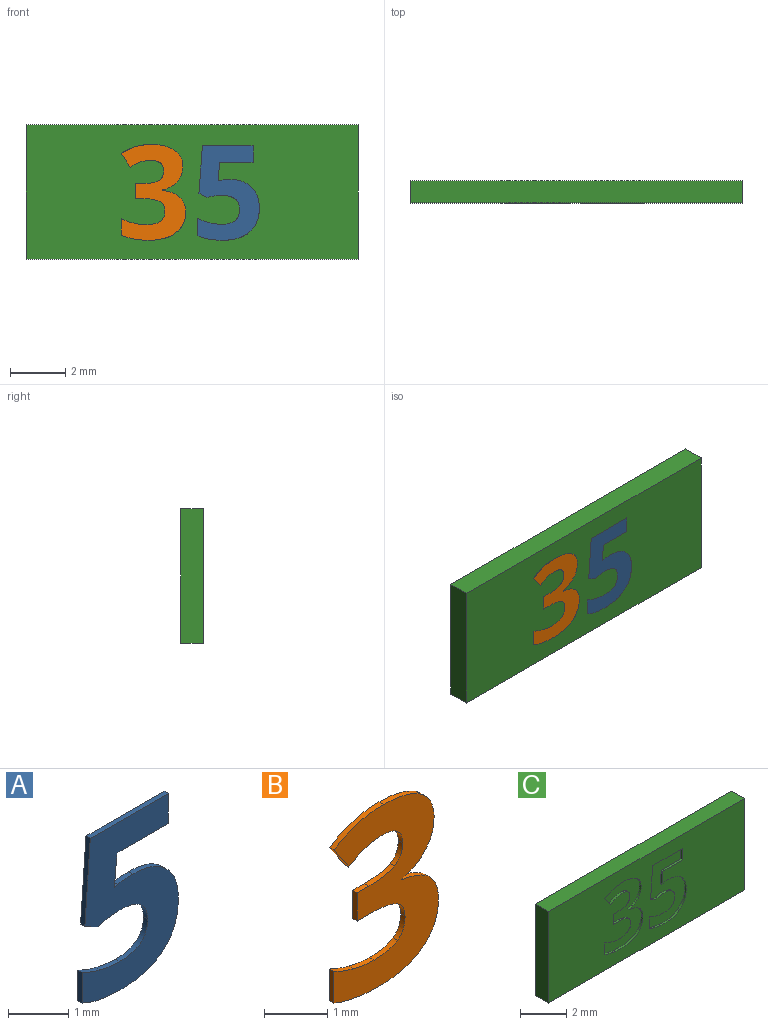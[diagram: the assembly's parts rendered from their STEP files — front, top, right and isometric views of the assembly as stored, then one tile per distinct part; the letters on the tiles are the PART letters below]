
ASSEMBLY  parts=3 mates=2
PART A: 22 faces, bbox 2.3x0.1x3.4 mm
  f0: plane 3.42x2.25mm, normal (0,-1,0), area 4.5mm2, adj f1,f2,f3,f4,f5,f6,f7,f8
  f1: plane 0.1x0.08mm, normal (-0.2,0,0.98), area 0mm2, adj f0,f2,f18,f20
  f2: plane 0.66x0.1mm, normal (1,0,-0.09), area 0.1mm2, adj f0,f1,f3,f18
  f3: plane 1.2x0.1mm, normal (0,0,-1), area 0.1mm2, adj f0,f2,f4,f18
  f4: plane 0.6x0.1mm, normal (1,0,0), area 0.1mm2, adj f0,f3,f5,f18
  f5: plane 1.83x0.1mm, normal (0,0,1), area 0.2mm2, adj f0,f4,f6,f18
  f6: plane 1.72x0.13mm, normal (-1,0,0.07), area 0.2mm2, adj f0,f5,f7,f18
  f7: plane 0.28x0.15mm, normal (-0.47,0,-0.88), area 0mm2, adj f0,f6,f8,f18
  f8: extruded ~0.24x0.1mm, area 0mm2, adj f0,f7,f9,f18
  f9: extruded ~0.27x0.1mm, area 0mm2, adj f0,f8,f10,f18
  f10: extruded ~0.68x0.51mm, area 0.1mm2, adj f0,f9,f11,f18
  f11: extruded ~0.65x0.54mm, area 0.1mm2, adj f0,f10,f12,f18
  f12: extruded ~0.46x0.1mm, area 0mm2, adj f0,f11,f13,f18
  f13: extruded ~0.42x0.16mm, area 0mm2, adj f0,f12,f14,f18
  f14: plane 0.62x0.1mm, normal (-1,0,0), area 0.1mm2, adj f0,f13,f15,f18
  f15: extruded ~0.91x0.18mm, area 0.1mm2, adj f0,f14,f16,f18
  f16: extruded ~1x0.3mm, area 0.1mm2, adj f0,f15,f17,f18
  f17: extruded ~0.87x0.35mm, area 0.1mm2, adj f0,f16,f18,f19
  f18: plane 3.42x2.25mm, normal (0,1,0), area 4.5mm2, adj f1,f2,f3,f4,f5,f6,f7,f8
  f19: extruded ~0.75x0.29mm, area 0.1mm2, adj f0,f17,f18,f21
  f20: extruded ~0.35x0.1mm, area 0mm2, adj f0,f1,f18,f21
  f21: extruded ~0.78x0.27mm, area 0.1mm2, adj f0,f18,f19,f20
PART B: 29 faces, bbox 2.3x0.1x3.5 mm
  f0: plane 3.47x2.33mm, normal (0,-1,0), area 4.3mm2, adj f1,f2,f3,f4,f5,f6,f7,f8
  f1: extruded ~0.83x0.21mm, area 0.1mm2, adj f0,f2,f25,f27
  f2: extruded ~1.1x0.33mm, area 0.1mm2, adj f0,f1,f3,f25
  f3: plane 0.49x0.33mm, normal (-0.83,0,-0.56), area 0.1mm2, adj f0,f2,f4,f25
  f4: extruded ~0.38x0.19mm, area 0mm2, adj f0,f3,f5,f25
  f5: extruded ~0.34x0.1mm, area 0mm2, adj f0,f4,f6,f25
  f6: extruded ~0.48x0.38mm, area 0.1mm2, adj f0,f5,f7,f25
  f7: extruded ~0.35x0.18mm, area 0mm2, adj f0,f6,f8,f25
  f8: extruded ~0.57x0.1mm, area 0.1mm2, adj f0,f7,f9,f25
  f9: plane 0.26x0.1mm, normal (0,0,1), area 0mm2, adj f0,f8,f10,f25
  f10: plane 0.55x0.1mm, normal (-1,0,0), area 0.1mm2, adj f0,f9,f11,f25
  f11: plane 0.26x0.1mm, normal (0,0,-1), area 0mm2, adj f0,f10,f12,f25
  f12: extruded ~0.62x0.1mm, area 0.1mm2, adj f0,f11,f13,f25
  f13: extruded ~0.34x0.19mm, area 0mm2, adj f0,f12,f14,f25
  f14: extruded ~0.39x0.17mm, area 0mm2, adj f0,f13,f15,f25
  f15: extruded ~0.52x0.12mm, area 0.1mm2, adj f0,f14,f16,f25
  f16: extruded ~0.47x0.1mm, area 0mm2, adj f0,f15,f17,f25
  f17: extruded ~0.43x0.16mm, area 0mm2, adj f0,f16,f18,f25
  f18: plane 0.61x0.1mm, normal (-1,0,0), area 0.1mm2, adj f0,f17,f19,f25
  f19: extruded ~0.97x0.18mm, area 0.1mm2, adj f0,f18,f20,f25
  f20: extruded ~1.01x0.27mm, area 0.1mm2, adj f0,f19,f21,f25
  f21: extruded ~0.76x0.35mm, area 0.1mm2, adj f0,f20,f22,f25
  f22: extruded ~0.53x0.21mm, area 0.1mm2, adj f0,f21,f23,f25
  f23: extruded ~0.62x0.25mm, area 0.1mm2, adj f0,f22,f24,f25
  f24: plane 0.1x0.01mm, normal (1,0,0), area 0mm2, adj f0,f23,f25,f26
  f25: plane 3.47x2.33mm, normal (0,1,0), area 4.3mm2, adj f1,f2,f3,f4,f5,f6,f7,f8
  f26: extruded ~0.54x0.3mm, area 0.1mm2, adj f0,f24,f25,f28
  f27: extruded ~0.59x0.3mm, area 0.1mm2, adj f0,f1,f25,f28
  f28: extruded ~0.54x0.19mm, area 0.1mm2, adj f0,f25,f26,f27
PART C: 55 faces, bbox 12x0.8x4.9 mm
  f0: plane 12x4.85mm, normal (0,-1,0), area 49.4mm2, adj f1,f2,f3,f4,f6,f7,f8,f9
  f1: plane 12x0.8mm, normal (0,0,-1), area 9.6mm2, adj f0,f2,f4,f5
  f2: plane 4.85x0.8mm, normal (1,0,0), area 3.9mm2, adj f0,f1,f3,f5
  f3: plane 12x0.8mm, normal (0,0,1), area 9.6mm2, adj f0,f2,f4,f5
  f4: plane 4.85x0.8mm, normal (-1,0,0), area 3.9mm2, adj f0,f1,f3,f5
  f5: plane 12x4.85mm, normal (0,1,0), area 58.2mm2, adj f1,f2,f3,f4
  f6: extruded ~0.35x0.1mm, area 0mm2, adj f0,f7,f25,f26
  f7: plane 0.1x0.08mm, normal (0.2,0,-0.98), area 0mm2, adj f0,f6,f8,f26
  f8: plane 0.66x0.1mm, normal (-1,0,0.09), area 0.1mm2, adj f0,f7,f9,f26
  f9: plane 1.2x0.1mm, normal (0,0,1), area 0.1mm2, adj f0,f8,f10,f26
  f10: plane 0.6x0.1mm, normal (-1,0,0), area 0.1mm2, adj f0,f9,f11,f26
  f11: plane 1.83x0.1mm, normal (0,0,-1), area 0.2mm2, adj f0,f10,f12,f26
  f12: plane 1.72x0.13mm, normal (1,0,-0.07), area 0.2mm2, adj f0,f11,f13,f26
  f13: plane 0.28x0.15mm, normal (0.47,0,0.88), area 0mm2, adj f0,f12,f14,f26
  f14: extruded ~0.24x0.1mm, area 0mm2, adj f0,f13,f15,f26
  f15: extruded ~0.27x0.1mm, area 0mm2, adj f0,f14,f16,f26
  f16: extruded ~0.68x0.51mm, area 0.1mm2, adj f0,f15,f17,f26
  f17: extruded ~0.65x0.54mm, area 0.1mm2, adj f0,f16,f18,f26
  f18: extruded ~0.46x0.1mm, area 0mm2, adj f0,f17,f19,f26
  f19: extruded ~0.42x0.16mm, area 0mm2, adj f0,f18,f20,f26
  f20: plane 0.62x0.1mm, normal (1,0,0), area 0.1mm2, adj f0,f19,f21,f26
  f21: extruded ~0.91x0.18mm, area 0.1mm2, adj f0,f20,f22,f26
  f22: extruded ~1x0.3mm, area 0.1mm2, adj f0,f21,f23,f26
  f23: extruded ~0.87x0.35mm, area 0.1mm2, adj f0,f22,f24,f26
  f24: extruded ~0.75x0.29mm, area 0.1mm2, adj f0,f23,f25,f26
  f25: extruded ~0.78x0.27mm, area 0.1mm2, adj f0,f6,f24,f26
  f26: plane 3.42x2.25mm, normal (0,-1,0), area 4.5mm2, adj f6,f7,f8,f9,f10,f11,f12,f13
  f27: extruded ~0.59x0.3mm, area 0.1mm2, adj f0,f28,f53,f54
  f28: extruded ~0.83x0.21mm, area 0.1mm2, adj f0,f27,f29,f54
  f29: extruded ~1.1x0.33mm, area 0.1mm2, adj f0,f28,f30,f54
  f30: plane 0.49x0.33mm, normal (0.83,0,0.56), area 0.1mm2, adj f0,f29,f31,f54
  f31: extruded ~0.38x0.19mm, area 0mm2, adj f0,f30,f32,f54
  f32: extruded ~0.34x0.1mm, area 0mm2, adj f0,f31,f33,f54
  f33: extruded ~0.48x0.38mm, area 0.1mm2, adj f0,f32,f34,f54
  f34: extruded ~0.35x0.18mm, area 0mm2, adj f0,f33,f35,f54
  f35: extruded ~0.57x0.1mm, area 0.1mm2, adj f0,f34,f36,f54
  f36: plane 0.26x0.1mm, normal (0,0,-1), area 0mm2, adj f0,f35,f37,f54
  f37: plane 0.55x0.1mm, normal (1,0,0), area 0.1mm2, adj f0,f36,f38,f54
  f38: plane 0.26x0.1mm, normal (0,0,1), area 0mm2, adj f0,f37,f39,f54
  f39: extruded ~0.62x0.1mm, area 0.1mm2, adj f0,f38,f40,f54
  f40: extruded ~0.34x0.19mm, area 0mm2, adj f0,f39,f41,f54
  f41: extruded ~0.39x0.17mm, area 0mm2, adj f0,f40,f42,f54
  f42: extruded ~0.52x0.12mm, area 0.1mm2, adj f0,f41,f43,f54
  f43: extruded ~0.47x0.1mm, area 0mm2, adj f0,f42,f44,f54
  f44: extruded ~0.43x0.16mm, area 0mm2, adj f0,f43,f45,f54
  f45: plane 0.61x0.1mm, normal (1,0,0), area 0.1mm2, adj f0,f44,f46,f54
  f46: extruded ~0.97x0.18mm, area 0.1mm2, adj f0,f45,f47,f54
  f47: extruded ~1.01x0.27mm, area 0.1mm2, adj f0,f46,f48,f54
  f48: extruded ~0.76x0.35mm, area 0.1mm2, adj f0,f47,f49,f54
  f49: extruded ~0.53x0.21mm, area 0.1mm2, adj f0,f48,f50,f54
  f50: extruded ~0.62x0.25mm, area 0.1mm2, adj f0,f49,f51,f54
  f51: plane 0.1x0.01mm, normal (-1,0,0), area 0mm2, adj f0,f50,f52,f54
  f52: extruded ~0.54x0.3mm, area 0.1mm2, adj f0,f51,f53,f54
  f53: extruded ~0.54x0.19mm, area 0.1mm2, adj f0,f27,f52,f54
  f54: plane 3.47x2.33mm, normal (0,-1,0), area 4.3mm2, adj f27,f28,f29,f30,f31,f32,f33,f34
PLACE A t=(-0.23,0.39,0)mm
PLACE B t=(-2.91,0.39,0)mm
PLACE C t=(-0.01,0.39,0)mm
MATE fastened B.f0 <-> C.f0  axis (0,-1,0) through (-2.57,-0.41,-1.57)mm
MATE fastened A.f0 <-> C.f0  axis (0,-1,0) through (0.18,-0.41,-1.57)mm
